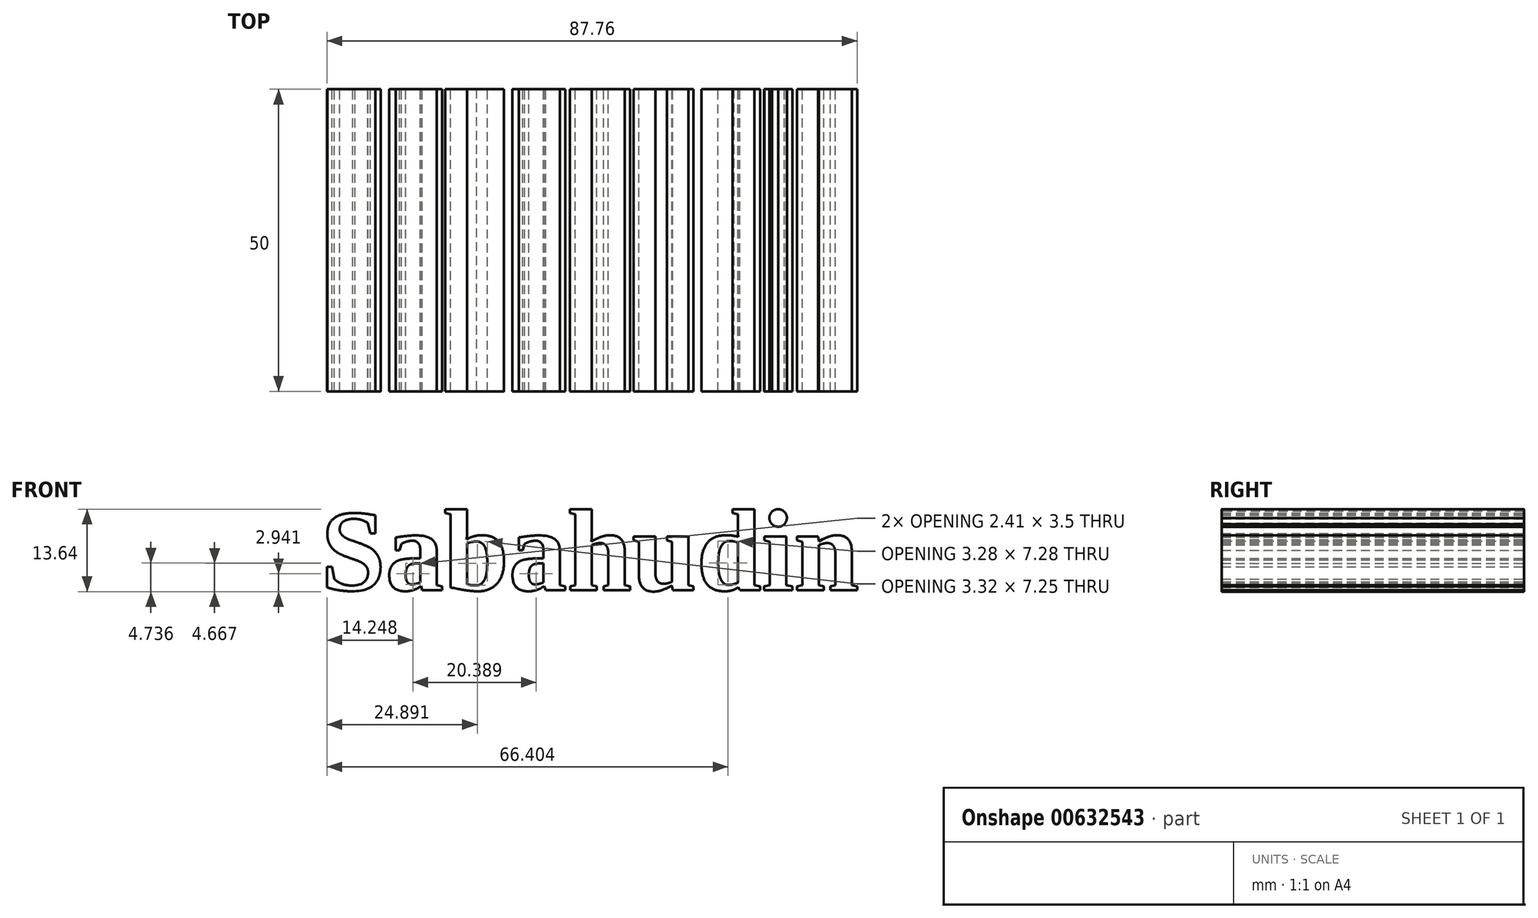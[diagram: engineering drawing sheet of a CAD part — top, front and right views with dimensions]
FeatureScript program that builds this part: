
annotation { "Feature Type Name" : "Feature", "Feature Type Description" : "" }
export const myFeature = defineFeature(function(context is Context, id is Id, definition is map)
    precondition{}
    {
        {
            var Q0;
            Q0=qCreatedBy(makeId("Front.planeOp"),FACE);
            var sketch = newSketch(context, id + "F0", { "sketchPlane" : qUnion([Q0])});
            skLineSegment(sketch, "E0.bottom", {"start": v(28.24, 100) * mm, "end": v(-71.76, 100) * mm});
            skLineSegment(sketch, "E0.top", {"start": v(28.24, 0) * mm, "end": v(-71.76, 0) * mm});
            skLineSegment(sketch, "E0.left", {"start": v(28.24, 100) * mm, "end": v(28.24, 0) * mm});
            skLineSegment(sketch, "E0.right", {"start": v(-71.76, 100) * mm, "end": v(-71.76, 0) * mm});
            skSolve(sketch);
        }
        {
            var Q0;
            Q0=makeQuery(id+"F0.imprint","IMPRINT",FACE,{"disambiguationData":[TD([[makeQuery(id+"F0.imprint","IMPRINT",EDGE,{"derivedFrom":sQuery(id+"F0.wireOp",EDGE,"E0.bottom")}),1.0]])]});
            var sketch = newSketch(context, id + "F1", { "sketchPlane" : qUnion([Q0])});
            skText(sketch, "E1", { "text": "Sabahudin", "fontName": "Tinos-Bold.ttf"});
            const initialGuessF1  = {"E1": [-0.0663, 0.04258, 1, 0, 0.0139]};
            skSetInitialGuess(sketch, initialGuessF1);
            skSolve(sketch);
        }
        {
            var Q0;
            Q0 = qSketchRegion(id + "F1", true);
            extrude(context, id + "F2", {"entities" : qUnion([Q0]), "depth" : 50 * mm, "offsetDistance" : 25 * mm});
        }
    });
